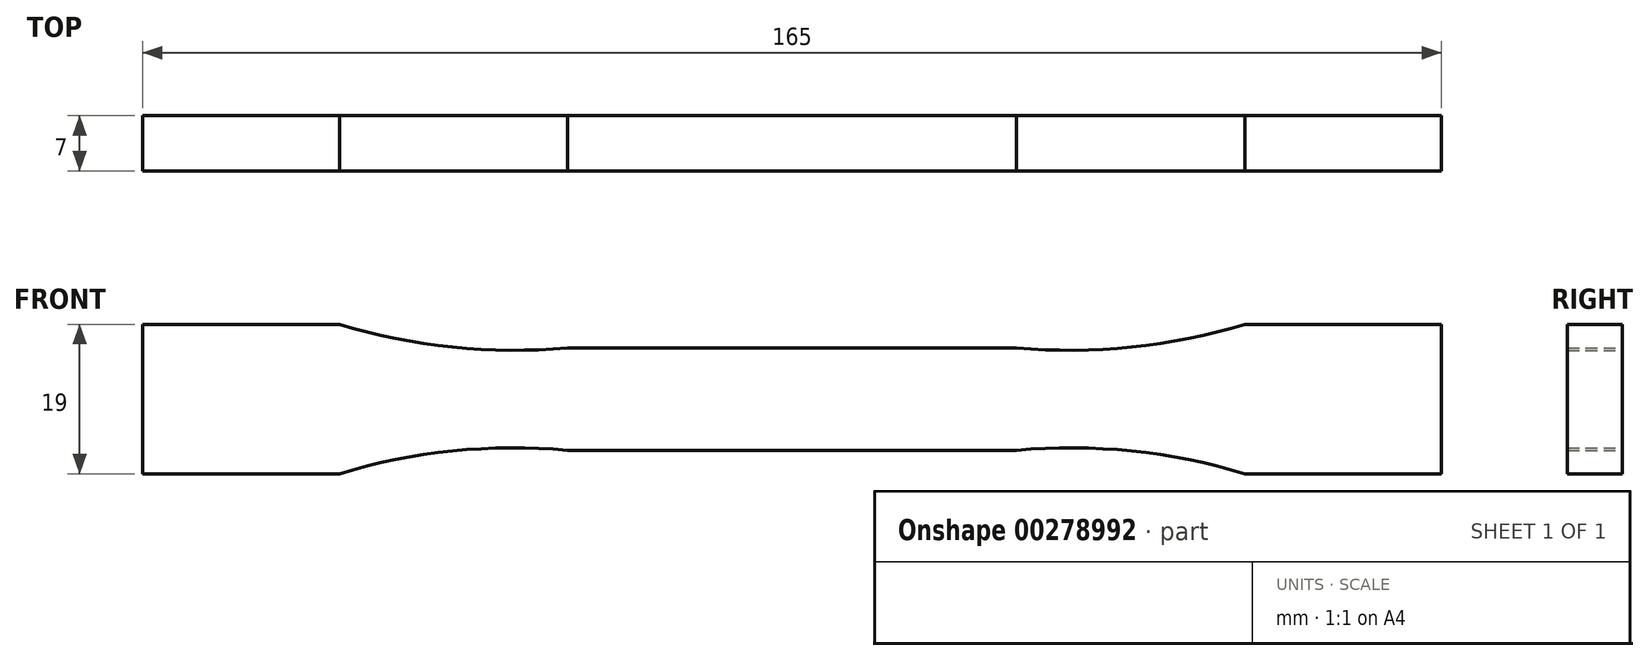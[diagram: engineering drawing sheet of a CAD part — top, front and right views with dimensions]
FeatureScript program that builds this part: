
annotation { "Feature Type Name" : "Feature", "Feature Type Description" : "" }
export const myFeature = defineFeature(function(context is Context, id is Id, definition is map)
    precondition{}
    {
        {
            var Q0;
            Q0=qCreatedBy(makeId("Front.planeOp"),FACE);
            var sketch = newSketch(context, id + "F0", { "sketchPlane" : qUnion([Q0])});
            skLineSegment(sketch, "E0", {"start": v(0, 6.5) * mm, "end": v(28.5, 6.5) * mm});
            skArc(sketch, "E1", {"start": v(28.5, 6.5) * mm, "mid": v(43.15, 6.6) * mm, "end": v(57.5, 9.5) * mm});
            skLineSegment(sketch, "E2", {"start": v(57.5, 9.5) * mm, "end": v(82.5, 9.5) * mm});
            skLineSegment(sketch, "E3.MirrorCS", {"start": v(57.5, -9.5) * mm, "end": v(82.5, -9.5) * mm});
            skLineSegment(sketch, "E4.MirrorCS", {"start": v(0, -6.5) * mm, "end": v(28.5, -6.5) * mm});
            skArc(sketch, "E5.MirrorCS", {"start": v(28.5, -6.5) * mm, "mid": v(43.15, -6.6) * mm, "end": v(57.5, -9.5) * mm});
            skArc(sketch, "E6.MirrorCS", {"start": v(-28.5, -6.5) * mm, "mid": v(-43.15, -6.6) * mm, "end": v(-57.5, -9.5) * mm});
            skLineSegment(sketch, "E7.MirrorCS", {"start": v(0, 6.5) * mm, "end": v(-28.5, 6.5) * mm});
            skArc(sketch, "E8.MirrorCS", {"start": v(-28.5, 6.5) * mm, "mid": v(-43.15, 6.6) * mm, "end": v(-57.5, 9.5) * mm});
            skLineSegment(sketch, "E9.MirrorCS", {"start": v(-57.5, 9.5) * mm, "end": v(-82.5, 9.5) * mm});
            skLineSegment(sketch, "E10.MirrorCS", {"start": v(-57.5, -9.5) * mm, "end": v(-82.5, -9.5) * mm});
            skLineSegment(sketch, "E11.MirrorCS", {"start": v(0, -6.5) * mm, "end": v(-28.5, -6.5) * mm});
            skLineSegment(sketch, "E12", {"start": v(82.5, 9.5) * mm, "end": v(82.5, -9.5) * mm});
            skLineSegment(sketch, "E13", {"start": v(-82.5, 9.5) * mm, "end": v(-82.5, -9.5) * mm});
            skSolve(sketch);
        }
        {
            var Q0;
            Q0=makeQuery(id+"F0.imprint","IMPRINT",FACE,{"disambiguationData":[TD([[makeQuery(id+"F0.imprint","IMPRINT",EDGE,{"derivedFrom":sQuery(id+"F0.wireOp",EDGE,"E0")}),-1.0]])]});
            extrude(context, id + "F1", {"entities" : qUnion([Q0]), "endBound" : BoundingType.SYMMETRIC, "depth" : 7 * mm});
        }
    });
